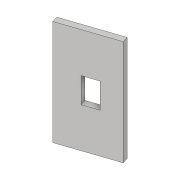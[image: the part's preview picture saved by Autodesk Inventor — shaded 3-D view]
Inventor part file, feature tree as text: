
AUTODESK INVENTOR PART (.ipt)
format: ipt  version: 2018.3 (Build 223284000, 284)  size: 93,184 bytes
history: native  units: in
note: dims shown in document units (in); Inventor stores cm internally (conversion verified against a paired STEP export)
features: extrude x2, sketch x2
ambient origin geometry x8: Origin, YZ Plane, XZ Plane, XY Plane, X Axis, Y Axis, Z Axis, Center Point
bodies: Solid1 (feature_tree)
feature tree (4):
  extrude  "Extrusion1"  Depth=0.118in
  extrude  "Extrusion2"  Depth=0.5in
  sketch  "Sketch1"  dims[d0=1.1in d3=2.079in d4=0.0in d5=0.118in]
  sketch  "Sketch2"  dims[d7=0.3in d8=0.5in d9=0.5in d10=0.3in d13=0.7895in d14=0.7895in d16=1.0in d17=0.0in d18=0.7393in]
